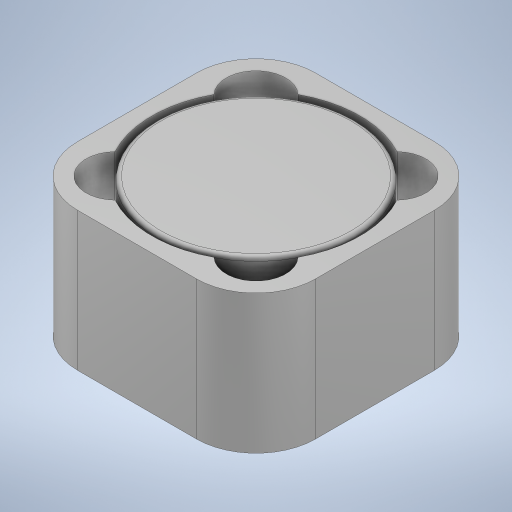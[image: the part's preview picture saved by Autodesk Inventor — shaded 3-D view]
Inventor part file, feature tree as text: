
AUTODESK INVENTOR PART (.ipt)
format: ipt  version: 2024.1 (Build 281209000, 209)  size: 255,488 bytes
history: native  units: mm
features: extrude x2, fillet x2, sketch x2, other x1
ambient origin geometry x8: Origin, YZ Plane, XZ Plane, XY Plane, X Axis, Y Axis, Z Axis, Center Point
bodies: Body1 (feature_tree)
feature tree (7):
  other  "ソリッド1"
  extrude  "押し出し1"  Depth=12.0mm
  fillet  "フィレット1"  Radius=7.0mm
  extrude  "押し出し2"  Depth=3.0mm
  fillet  "フィレット2"  Radius=10.0mm
  sketch  "スケッチ1"
  sketch  "スケッチ2"
